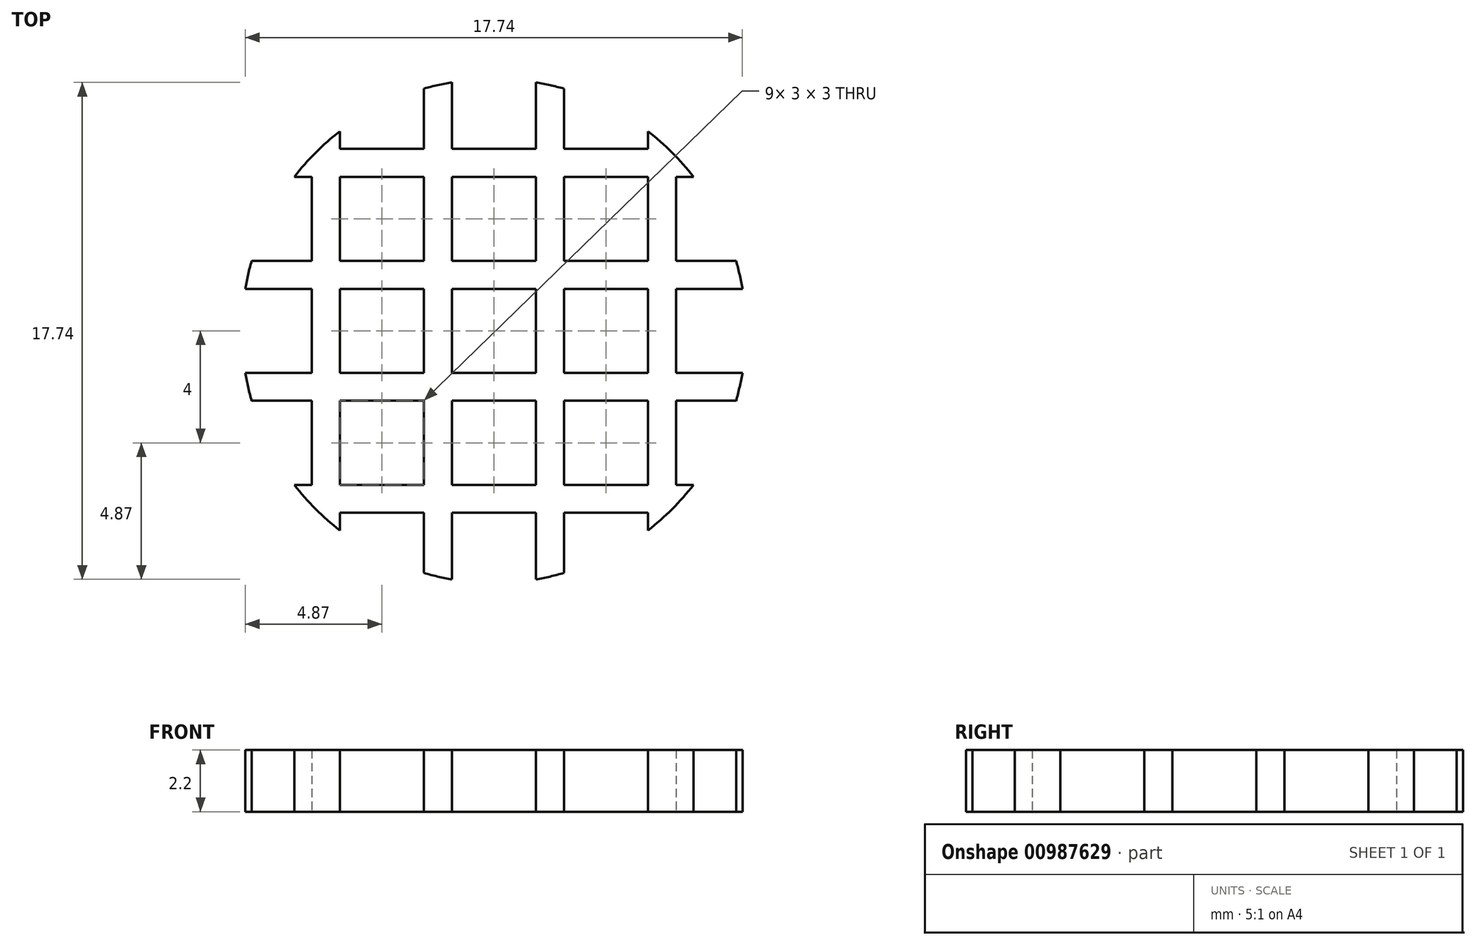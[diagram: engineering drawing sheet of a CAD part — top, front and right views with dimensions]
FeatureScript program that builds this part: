
annotation { "Feature Type Name" : "Feature", "Feature Type Description" : "" }
export const myFeature = defineFeature(function(context is Context, id is Id, definition is map)
    precondition{}
    {
        {
            var Q0;
            Q0=qCreatedBy(makeId("Top.planeOp"),FACE);
            var sketch = newSketch(context, id + "F0", { "sketchPlane" : qUnion([Q0])});
            skLineSegment(sketch, "E0.1.0.0", {"start": v(4, 3) * mm, "end": v(1, 3) * mm});
            skLineSegment(sketch, "E0.1.0.1", {"start": v(1, 2.38) * mm, "end": v(1, 3) * mm});
            skLineSegment(sketch, "E0.1.0.3", {"start": v(4, 0.85) * mm, "end": v(4, 3) * mm});
            skLineSegment(sketch, "E0.2.0.0", {"start": v(8, 3) * mm, "end": v(5, 3) * mm});
            skLineSegment(sketch, "E0.2.0.1", {"start": v(5, 0.63) * mm, "end": v(5, 3) * mm});
            skLineSegment(sketch, "E0.2.0.3", {"start": v(8, 0.63) * mm, "end": v(8, 3) * mm});
            skLineSegment(sketch, "E0.3.0.0", {"start": v(12, 3) * mm, "end": v(9, 3) * mm});
            skLineSegment(sketch, "E0.3.0.1", {"start": v(9, 0.85) * mm, "end": v(9, 3) * mm});
            skLineSegment(sketch, "E1.0.1.0", {"start": v(15.15, 7) * mm, "end": v(13, 7) * mm});
            skLineSegment(sketch, "E1.0.1.2", {"start": v(12, 4) * mm, "end": v(12, 7) * mm});
            skLineSegment(sketch, "E1.0.1.3", {"start": v(4, 4) * mm, "end": v(1, 4) * mm});
            skLineSegment(sketch, "E1.0.1.4", {"start": v(12, 7) * mm, "end": v(9, 7) * mm});
            skLineSegment(sketch, "E1.0.1.5", {"start": v(5, 4) * mm, "end": v(5, 7) * mm});
            skLineSegment(sketch, "E1.0.1.8", {"start": v(4, 7) * mm, "end": v(1, 7) * mm});
            skLineSegment(sketch, "E1.0.1.9", {"start": v(0, 4) * mm, "end": v(-0.62, 4) * mm});
            skLineSegment(sketch, "E1.0.1.10", {"start": v(8, 4) * mm, "end": v(8, 7) * mm});
            skLineSegment(sketch, "E1.0.1.11", {"start": v(9, 4) * mm, "end": v(9, 7) * mm});
            skLineSegment(sketch, "E1.0.1.12", {"start": v(1, 4) * mm, "end": v(1, 7) * mm});
            skLineSegment(sketch, "E1.0.1.13", {"start": v(0, 4) * mm, "end": v(0, 7) * mm});
            skLineSegment(sketch, "E1.0.1.14", {"start": v(12, 4) * mm, "end": v(9, 4) * mm});
            skLineSegment(sketch, "E1.0.1.15", {"start": v(13.62, 4) * mm, "end": v(13, 4) * mm});
            skLineSegment(sketch, "E1.0.1.16", {"start": v(8, 4) * mm, "end": v(5, 4) * mm});
            skLineSegment(sketch, "E1.0.1.17", {"start": v(4, 4) * mm, "end": v(4, 7) * mm});
            skLineSegment(sketch, "E1.0.1.18", {"start": v(8, 7) * mm, "end": v(5, 7) * mm});
            skLineSegment(sketch, "E1.0.1.19", {"start": v(13, 4) * mm, "end": v(13, 7) * mm});
            skLineSegment(sketch, "E1.0.2.0", {"start": v(15.37, 11) * mm, "end": v(13, 11) * mm});
            skLineSegment(sketch, "E1.0.2.2", {"start": v(12, 8) * mm, "end": v(12, 11) * mm});
            skLineSegment(sketch, "E1.0.2.3", {"start": v(4, 8) * mm, "end": v(1, 8) * mm});
            skLineSegment(sketch, "E1.0.2.4", {"start": v(12, 11) * mm, "end": v(9, 11) * mm});
            skLineSegment(sketch, "E1.0.2.5", {"start": v(5, 8) * mm, "end": v(5, 11) * mm});
            skLineSegment(sketch, "E1.0.2.8", {"start": v(4, 11) * mm, "end": v(1, 11) * mm});
            skLineSegment(sketch, "E1.0.2.9", {"start": v(0, 8) * mm, "end": v(-2.37, 8) * mm});
            skLineSegment(sketch, "E1.0.2.10", {"start": v(8, 8) * mm, "end": v(8, 11) * mm});
            skLineSegment(sketch, "E1.0.2.11", {"start": v(9, 8) * mm, "end": v(9, 11) * mm});
            skLineSegment(sketch, "E1.0.2.12", {"start": v(1, 8) * mm, "end": v(1, 11) * mm});
            skLineSegment(sketch, "E1.0.2.13", {"start": v(0, 8) * mm, "end": v(0, 11) * mm});
            skLineSegment(sketch, "E1.0.2.14", {"start": v(12, 8) * mm, "end": v(9, 8) * mm});
            skLineSegment(sketch, "E1.0.2.15", {"start": v(15.37, 8) * mm, "end": v(13, 8) * mm});
            skLineSegment(sketch, "E1.0.2.16", {"start": v(8, 8) * mm, "end": v(5, 8) * mm});
            skLineSegment(sketch, "E1.0.2.17", {"start": v(4, 8) * mm, "end": v(4, 11) * mm});
            skLineSegment(sketch, "E1.0.2.18", {"start": v(8, 11) * mm, "end": v(5, 11) * mm});
            skLineSegment(sketch, "E1.0.2.19", {"start": v(13, 8) * mm, "end": v(13, 11) * mm});
            skLineSegment(sketch, "E1.0.2.20", {"start": v(0, 11) * mm, "end": v(-2.37, 11) * mm});
            skLineSegment(sketch, "E1.0.3.2", {"start": v(12, 12) * mm, "end": v(12, 15) * mm});
            skLineSegment(sketch, "E1.0.3.3", {"start": v(4, 12) * mm, "end": v(1, 12) * mm});
            skLineSegment(sketch, "E1.0.3.4", {"start": v(12, 15) * mm, "end": v(9, 15) * mm});
            skLineSegment(sketch, "E1.0.3.5", {"start": v(5, 12) * mm, "end": v(5, 15) * mm});
            skLineSegment(sketch, "E1.0.3.8", {"start": v(4, 15) * mm, "end": v(1, 15) * mm});
            skLineSegment(sketch, "E1.0.3.9", {"start": v(0, 12) * mm, "end": v(-2.15, 12) * mm});
            skLineSegment(sketch, "E1.0.3.10", {"start": v(8, 12) * mm, "end": v(8, 15) * mm});
            skLineSegment(sketch, "E1.0.3.11", {"start": v(9, 12) * mm, "end": v(9, 15) * mm});
            skLineSegment(sketch, "E1.0.3.12", {"start": v(1, 12) * mm, "end": v(1, 15) * mm});
            skLineSegment(sketch, "E1.0.3.13", {"start": v(0, 12) * mm, "end": v(0, 15) * mm});
            skLineSegment(sketch, "E1.0.3.14", {"start": v(12, 12) * mm, "end": v(9, 12) * mm});
            skLineSegment(sketch, "E1.0.3.15", {"start": v(15.15, 12) * mm, "end": v(13, 12) * mm});
            skLineSegment(sketch, "E1.0.3.16", {"start": v(8, 12) * mm, "end": v(5, 12) * mm});
            skLineSegment(sketch, "E1.0.3.17", {"start": v(4, 12) * mm, "end": v(4, 15) * mm});
            skLineSegment(sketch, "E1.0.3.18", {"start": v(8, 15) * mm, "end": v(5, 15) * mm});
            skLineSegment(sketch, "E1.0.3.19", {"start": v(13, 12) * mm, "end": v(13, 15) * mm});
            skLineSegment(sketch, "E1.0.3.20", {"start": v(0, 15) * mm, "end": v(-0.62, 15) * mm});
            skLineSegment(sketch, "E1.0.4.2", {"start": v(12, 16) * mm, "end": v(12, 16.62) * mm});
            skLineSegment(sketch, "E1.0.4.3", {"start": v(4, 16) * mm, "end": v(1, 16) * mm});
            skLineSegment(sketch, "E1.0.4.5", {"start": v(5, 16) * mm, "end": v(5, 18.37) * mm});
            skLineSegment(sketch, "E1.0.4.10", {"start": v(8, 16) * mm, "end": v(8, 18.37) * mm});
            skLineSegment(sketch, "E1.0.4.11", {"start": v(9, 16) * mm, "end": v(9, 18.15) * mm});
            skLineSegment(sketch, "E1.0.4.12", {"start": v(1, 16) * mm, "end": v(1, 16.62) * mm});
            skLineSegment(sketch, "E1.0.4.14", {"start": v(12, 16) * mm, "end": v(9, 16) * mm});
            skLineSegment(sketch, "E1.0.4.16", {"start": v(8, 16) * mm, "end": v(5, 16) * mm});
            skLineSegment(sketch, "E1.0.4.17", {"start": v(4, 16) * mm, "end": v(4, 18.15) * mm});
            skArc(sketch, "E2", {"start": v(-2.15, 12) * mm, "mid": v(-2.27, 11.5) * mm, "end": v(-2.37, 11) * mm});
            skLineSegment(sketch, "E3", {"start": v(13, 15) * mm, "end": v(13.62, 15) * mm});
            skLineSegment(sketch, "E4", {"start": v(12, 3) * mm, "end": v(12, 2.38) * mm});
            skLineSegment(sketch, "E5", {"start": v(0, 7) * mm, "end": v(-2.15, 7) * mm});
            skArc(sketch, "E6.trimOffspring", {"start": v(1, 16.62) * mm, "mid": v(0.14, 15.86) * mm, "end": v(-0.62, 15) * mm});
            skArc(sketch, "E7.trimOffspring", {"start": v(5, 18.37) * mm, "mid": v(4.5, 18.27) * mm, "end": v(4, 18.15) * mm});
            skArc(sketch, "E8.trimOffspring", {"start": v(9, 18.15) * mm, "mid": v(8.5, 18.27) * mm, "end": v(8, 18.37) * mm});
            skArc(sketch, "E9.trimOffspring", {"start": v(13.62, 15) * mm, "mid": v(12.86, 15.86) * mm, "end": v(12, 16.62) * mm});
            skArc(sketch, "E10.trimOffspring", {"start": v(15.37, 11) * mm, "mid": v(15.27, 11.5) * mm, "end": v(15.15, 12) * mm});
            skArc(sketch, "E11.trimOffspring", {"start": v(15.15, 7) * mm, "mid": v(15.27, 7.5) * mm, "end": v(15.37, 8) * mm});
            skArc(sketch, "E12.trimOffspring", {"start": v(12, 2.38) * mm, "mid": v(12.86, 3.14) * mm, "end": v(13.62, 4) * mm});
            skArc(sketch, "E13.trimOffspring", {"start": v(8, 0.63) * mm, "mid": v(8.5, 0.73) * mm, "end": v(9, 0.85) * mm});
            skArc(sketch, "E14.trimOffspring", {"start": v(4, 0.85) * mm, "mid": v(4.5, 0.73) * mm, "end": v(5, 0.63) * mm});
            skArc(sketch, "E15.trimOffspring", {"start": v(-0.62, 4) * mm, "mid": v(0.14, 3.14) * mm, "end": v(1, 2.38) * mm});
            skArc(sketch, "E16.trimOffspring", {"start": v(-2.37, 8) * mm, "mid": v(-2.27, 7.5) * mm, "end": v(-2.15, 7) * mm});
            skSolve(sketch);
        }
        {
            var Q0;
            Q0 = qSketchRegion(id + "F0", true);
            extrude(context, id + "F1", {"entities" : qUnion([Q0]), "depth" : 2.2 * mm, "offsetDistance" : 25 * mm});
        }
    });
